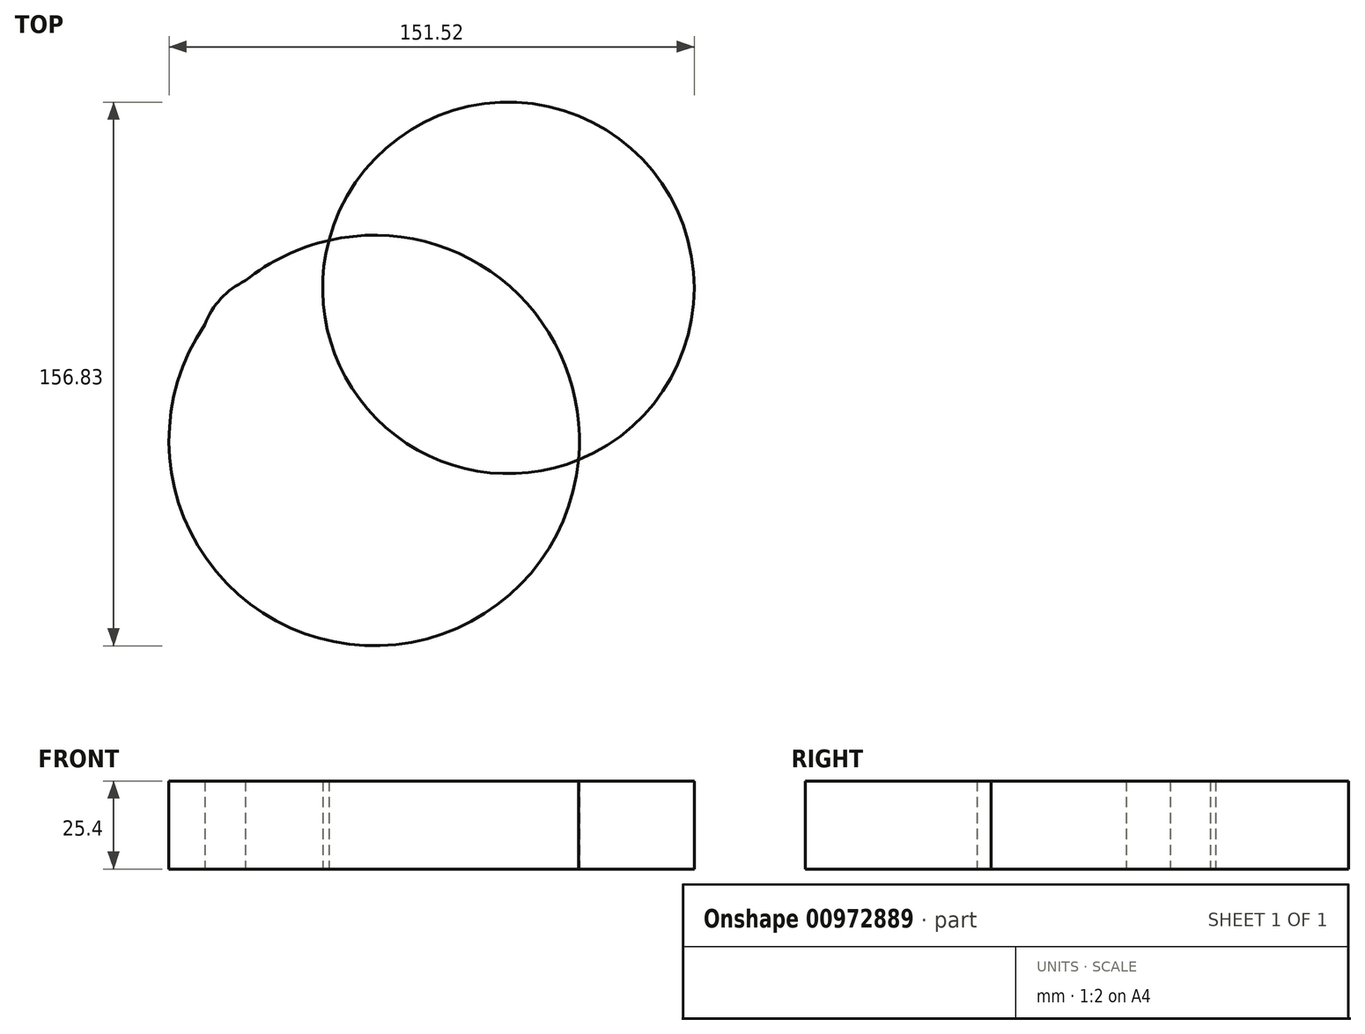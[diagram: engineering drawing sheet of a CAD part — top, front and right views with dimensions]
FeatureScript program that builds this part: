
annotation { "Feature Type Name" : "Feature", "Feature Type Description" : "" }
export const myFeature = defineFeature(function(context is Context, id is Id, definition is map)
    precondition{}
    {
        {
            var Q0;
            Q0=qCreatedBy(makeId("Top.planeOp"),FACE);
            var sketch = newSketch(context, id + "F0", { "sketchPlane" : qUnion([Q0])});
            skCircle(sketch, "E0", {"center": v(27.65, 37.17) * mm, "radius": 53.6 * mm});
            skPoint(sketch, "E0.first.point", {"position": v(-17.84, 8.83) * mm});
            skPoint(sketch, "E0.second.point", {"position": v(-25.84, 40.5) * mm});
            skPoint(sketch, "E0.third.point", {"position": v(39.17, -15.17) * mm});
            skCircle(sketch, "E1", {"center": v(-38.53, 18.55) * mm, "radius": 22.86 * mm});
            skPoint(sketch, "E1.second.point", {"position": v(-60.84, 23.5) * mm});
            skPoint(sketch, "E1.third.point", {"position": v(-32.17, 40.5) * mm});
            skCircle(sketch, "E2", {"center": v(-11.06, -6.85) * mm, "radius": 59.21 * mm});
            skPoint(sketch, "E2.first.point", {"position": v(-48.23, 39.25) * mm});
            skPoint(sketch, "E2.second.point", {"position": v(33.5, -45.84) * mm});
            skPoint(sketch, "E2.third.point", {"position": v(-64.84, -31.63) * mm});
            skSolve(sketch);
        }
        {
            var Q0;
            {var subQ0=sQuery(id+"F0.wireOp",EDGE,"E2");var subQ1=sQuery(id+"F0.wireOp",EDGE,"E0");var subQ2=makeQuery(id+"F0.imprint","INTERSECT",VERTEX,{"disambiguationData":[OD(0.0)],"derivedFrom":[subQ1,subQ0]});Q0=makeQuery(id+"F0.imprint","IMPRINT",FACE,{"disambiguationData":[TD([[makeQuery(id+"F0.imprint","IMPRINT",EDGE,{"disambiguationData":[TD([[subQ2,1.0]])],"derivedFrom":subQ1}),1.0]])]});}
            var Q1;
            {var subQ0=sQuery(id+"F0.wireOp",EDGE,"E2");var subQ1=sQuery(id+"F0.wireOp",EDGE,"E1");var subQ2=makeQuery(id+"F0.imprint","INTERSECT",VERTEX,{"disambiguationData":[OD(0.0)],"derivedFrom":[subQ1,subQ0]});Q1=makeQuery(id+"F0.imprint","IMPRINT",FACE,{"disambiguationData":[TD([[makeQuery(id+"F0.imprint","IMPRINT",EDGE,{"disambiguationData":[TD([[subQ2,-1.0]])],"derivedFrom":subQ1}),1.0]])]});}
            var Q2;
            {var subQ0=sQuery(id+"F0.wireOp",EDGE,"E2");var subQ1=sQuery(id+"F0.wireOp",EDGE,"E0");var subQ2=makeQuery(id+"F0.imprint","INTERSECT",VERTEX,{"disambiguationData":[OD(0.0)],"derivedFrom":[subQ1,subQ0]});Q2=makeQuery(id+"F0.imprint","IMPRINT",FACE,{"disambiguationData":[TD([[makeQuery(id+"F0.imprint","IMPRINT",EDGE,{"disambiguationData":[TD([[subQ2,-1.0]])],"derivedFrom":subQ1}),-1.0]])]});}
            var Q3;
            {var subQ0=sQuery(id+"F0.wireOp",EDGE,"E2");var subQ1=sQuery(id+"F0.wireOp",EDGE,"E0");var subQ2=makeQuery(id+"F0.imprint","INTERSECT",VERTEX,{"disambiguationData":[OD(1.0)],"derivedFrom":[subQ1,subQ0]});Q3=makeQuery(id+"F0.imprint","IMPRINT",FACE,{"disambiguationData":[TD([[makeQuery(id+"F0.imprint","IMPRINT",EDGE,{"disambiguationData":[TD([[subQ2,1.0]])],"derivedFrom":subQ1}),-1.0]])]});}
            var Q4;
            {var subQ0=sQuery(id+"F0.wireOp",EDGE,"E1");var subQ1=sQuery(id+"F0.wireOp",EDGE,"E0");var subQ2=makeQuery(id+"F0.imprint","INTERSECT",VERTEX,{"disambiguationData":[OD(0.0)],"derivedFrom":[subQ1,subQ0]});Q4=makeQuery(id+"F0.imprint","IMPRINT",FACE,{"disambiguationData":[TD([[makeQuery(id+"F0.imprint","IMPRINT",EDGE,{"disambiguationData":[TD([[subQ2,-1.0]])],"derivedFrom":subQ1}),-1.0]])]});}
            extrude(context, id + "F1", {"entities" : qUnion([Q0, Q1, Q2, Q3, Q4]), "depth" : 25.4 * mm, "offsetDistance" : 25.4 * mm});
        }
    });
